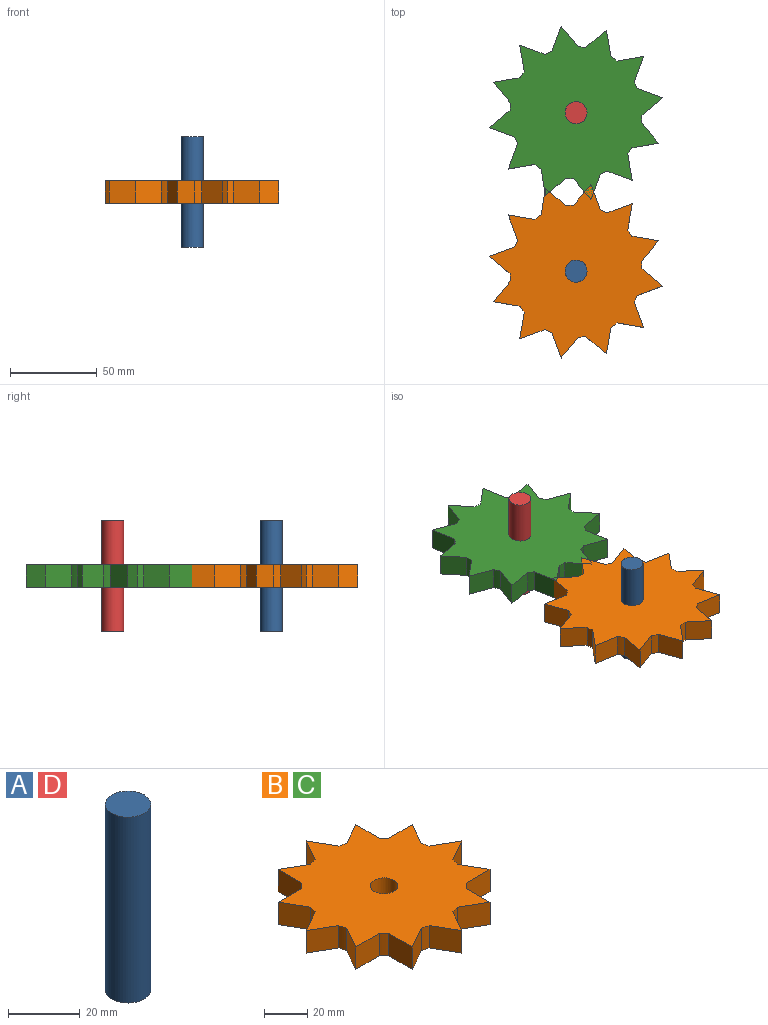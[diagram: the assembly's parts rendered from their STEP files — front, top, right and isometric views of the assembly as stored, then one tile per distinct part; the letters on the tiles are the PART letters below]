
ASSEMBLY  parts=4 mates=3
PART A: 3 faces, bbox 12.7x12.7x63.5 mm
  f0: cylinder r=6.35mm len=63.5mm, axis (0,0,-1), area 2533.5mm2, adj f1,f2
  f1: plane 12.7x12.7mm, normal (0,0,1), area 126.7mm2, adj f0
  f2: plane 12.7x12.7mm, normal (0,0,-1), area 126.7mm2, adj f0
PART B: 39 faces, bbox 101.6x101.6x12.7 mm
  f0: cylinder r=38.1mm len=12.7mm, axis (0,0,-1), area 53.9mm2, adj f12,f13,f15,f36
  f1: cylinder r=38.1mm len=12.7mm, axis (0,0,-1), area 53.9mm2, adj f12,f13,f35,f37
  f2: cylinder r=38.1mm len=12.7mm, axis (0,0,-1), area 53.9mm2, adj f12,f13,f33,f34
  f3: cylinder r=38.1mm len=12.7mm, axis (0,0,-1), area 53.9mm2, adj f12,f13,f31,f32
  f4: cylinder r=38.1mm len=12.7mm, axis (0,0,-1), area 53.9mm2, adj f12,f13,f29,f30
  f5: cylinder r=38.1mm len=12.7mm, axis (0,0,-1), area 53.9mm2, adj f12,f13,f27,f28
  f6: cylinder r=38.1mm len=12.7mm, axis (0,0,-1), area 53.9mm2, adj f12,f13,f25,f26
  f7: cylinder r=38.1mm len=12.7mm, axis (0,0,-1), area 53.9mm2, adj f12,f13,f23,f24
  f8: cylinder r=38.1mm len=12.7mm, axis (0,0,-1), area 53.9mm2, adj f12,f13,f21,f22
  f9: cylinder r=38.1mm len=12.7mm, axis (0,0,-1), area 53.9mm2, adj f12,f13,f19,f20
  f10: cylinder r=38.1mm len=12.7mm, axis (0,0,-1), area 53.9mm2, adj f12,f13,f17,f18
  f11: cylinder r=38.1mm len=12.7mm, axis (0,0,-1), area 53.9mm2, adj f12,f13,f14,f16
  f12: plane 101.6x101.6mm, normal (0,0,1), area 5596.7mm2, adj f0,f1,f2,f3,f4,f5,f6,f7
  f13: plane 101.6x101.6mm, normal (0,0,-1), area 5596.7mm2, adj f0,f1,f2,f3,f4,f5,f6,f7
  f14: plane 13.51x12.7mm, normal (0.87,0.5,0), area 198.1mm2, adj f11,f12,f13,f15
  f15: plane 13.51x12.7mm, normal (-0.87,0.5,0), area 198.1mm2, adj f0,f12,f13,f14
  f16: plane 13.51x12.7mm, normal (-0.5,0.87,0), area 198.1mm2, adj f11,f12,f13,f17
  f17: plane 15.6x12.7mm, normal (1,0,0), area 198.1mm2, adj f10,f12,f13,f16
  f18: plane 15.6x12.7mm, normal (0,1,0), area 198.1mm2, adj f10,f12,f13,f19
  f19: plane 13.51x12.7mm, normal (0.87,-0.5,0), area 198.1mm2, adj f9,f12,f13,f18
  f20: plane 13.51x12.7mm, normal (0.5,0.87,0), area 198.1mm2, adj f9,f12,f13,f21
  f21: plane 13.51x12.7mm, normal (0.5,-0.87,0), area 198.1mm2, adj f8,f12,f13,f20
  f22: plane 13.51x12.7mm, normal (0.87,0.5,0), area 198.1mm2, adj f8,f12,f13,f23
  f23: plane 15.6x12.7mm, normal (0,-1,0), area 198.1mm2, adj f7,f12,f13,f22
  f24: plane 15.6x12.7mm, normal (1,0,0), area 198.1mm2, adj f7,f12,f13,f25
  f25: plane 13.51x12.7mm, normal (-0.5,-0.87,0), area 198.1mm2, adj f6,f12,f13,f24
  f26: plane 13.51x12.7mm, normal (0.87,-0.5,0), area 198.1mm2, adj f6,f12,f13,f27
  f27: plane 13.51x12.7mm, normal (-0.87,-0.5,0), area 198.1mm2, adj f5,f12,f13,f26
  f28: plane 13.51x12.7mm, normal (0.5,-0.87,0), area 198.1mm2, adj f5,f12,f13,f29
  f29: plane 15.6x12.7mm, normal (-1,0,0), area 198.1mm2, adj f4,f12,f13,f28
  f30: plane 15.6x12.7mm, normal (0,-1,0), area 198.1mm2, adj f4,f12,f13,f31
  f31: plane 13.51x12.7mm, normal (-0.87,0.5,0), area 198.1mm2, adj f3,f12,f13,f30
  f32: plane 13.51x12.7mm, normal (-0.5,-0.87,0), area 198.1mm2, adj f3,f12,f13,f33
  f33: plane 13.51x12.7mm, normal (-0.5,0.87,0), area 198.1mm2, adj f2,f12,f13,f32
  f34: plane 13.51x12.7mm, normal (-0.87,-0.5,0), area 198.1mm2, adj f2,f12,f13,f35
  f35: plane 15.6x12.7mm, normal (0,1,0), area 198.1mm2, adj f1,f12,f13,f34
  f36: plane 13.51x12.7mm, normal (0.5,0.87,0), area 198.1mm2, adj f0,f12,f13,f37
  f37: plane 15.6x12.7mm, normal (-1,0,0), area 198.1mm2, adj f1,f12,f13,f36
  f38: cylinder r=6.35mm len=12.7mm, axis (0,0,1), area 506.7mm2, adj f12,f13
PART C: same geometry as B
PART D: same geometry as A
PLACE A t=(0,-91.44,0)mm
PLACE B rot(axis=(0,0,1),20.3deg) t=(0,-91.44,0)mm
PLACE C rot(axis=(0,0,-1),20.3deg) t=(0,0,0)mm
PLACE D at identity fixed
MATE fastened D.f0 <-> A.f1  axis (0,0,1) through (0,0,38.1)mm
MATE revolute C.f38 <-> D.f0  axis (0,0,1) through (0,0,6.35)mm
MATE revolute A.f0 <-> B.f38  axis (0,0,-1) through (0,-91.44,6.35)mm
